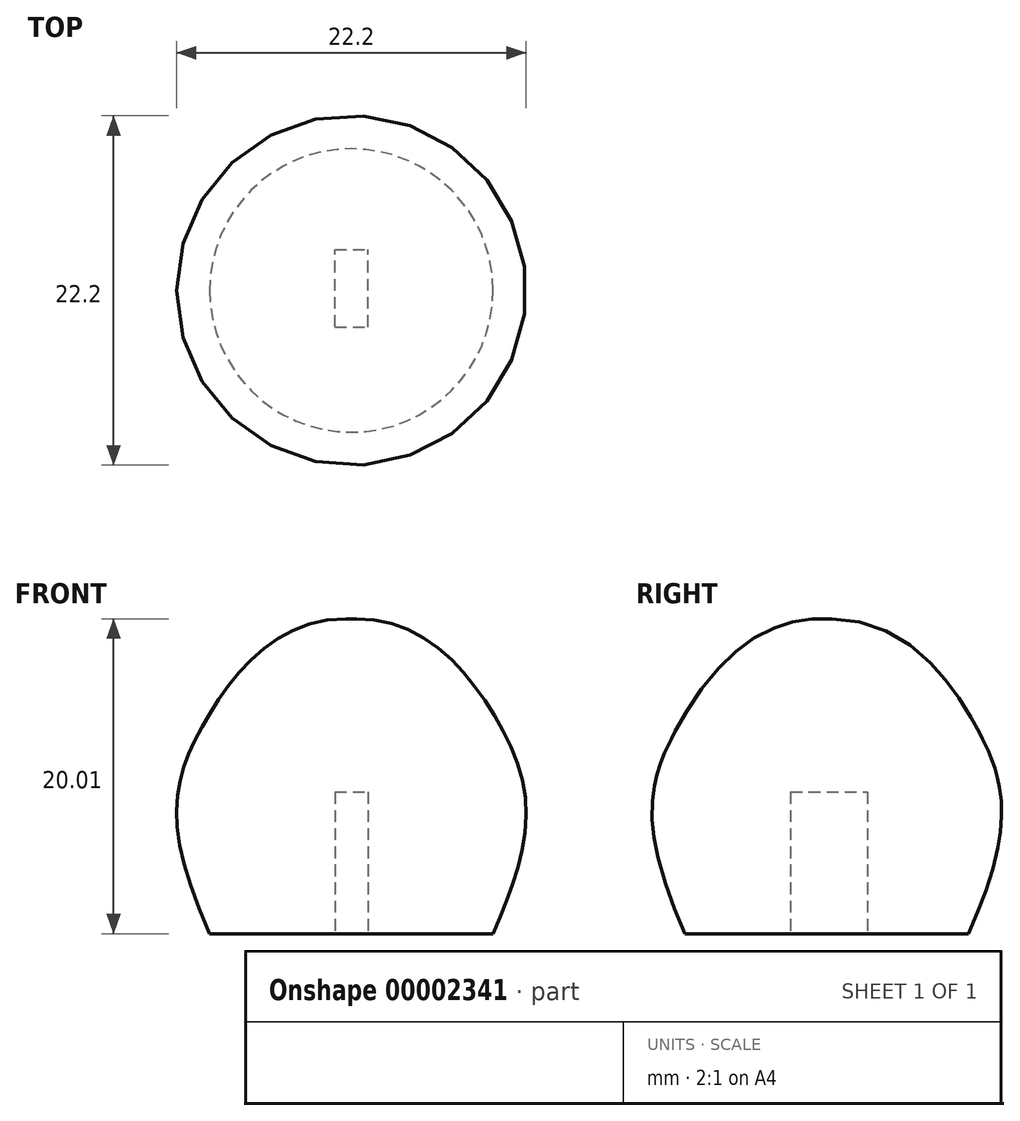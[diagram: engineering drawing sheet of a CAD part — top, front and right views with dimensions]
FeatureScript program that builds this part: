
annotation { "Feature Type Name" : "Feature", "Feature Type Description" : "" }
export const myFeature = defineFeature(function(context is Context, id is Id, definition is map)
    precondition{}
    {
        {
            var Q0;
            Q0=qCreatedBy(makeId("Front.planeOp"),FACE);
            var sketch = newSketch(context, id + "F0", { "sketchPlane" : qUnion([Q0])});
            skFitSpline(sketch, "E0", {"points": [v(-9, 0) * mm, v(-9.53, 13.06) * mm, v(0, 20) * mm], "startDerivative": vector(-17.7, 39.61) * mm, "endDerivative": vector(29.7, -1.1) * mm});
            skLineSegment(sketch, "E1", {"start": v(0, 20) * mm, "end": v(0, 0) * mm});
            skLineSegment(sketch, "E2", {"start": v(0, 0) * mm, "end": v(-9, 0) * mm});
            skSolve(sketch);
        }
        {
            var Q0;
            Q0 = qSketchRegion(id + "F0", true);
            var Q1;
            Q1=sQuery(id+"F0.wireOp",EDGE,"E1");
            revolve(context, id + "F1", {"entities" : qUnion([Q0]), "axis" : qUnion([Q1]), "revolveType" : RevolveType.FULL});
        }
        {
            var Q0;
            Q0=makeQuery(id+"F1.opRevolve","SWEPT_FACE",FACE,{"disambiguationData":[OSD([sQuery(id+"F0.wireOp",EDGE,"E2")])]});
            var sketch = newSketch(context, id + "F2", { "sketchPlane" : qUnion([Q0])});
            skLineSegment(sketch, "E3.bottom", {"start": v(-1.05, 2.3) * mm, "end": v(1.05, 2.3) * mm});
            skLineSegment(sketch, "E3.top", {"start": v(-1.05, -2.6) * mm, "end": v(1.05, -2.6) * mm});
            skLineSegment(sketch, "E3.left", {"start": v(-1.05, 2.3) * mm, "end": v(-1.05, -2.6) * mm});
            skLineSegment(sketch, "E3.right", {"start": v(1.05, 2.3) * mm, "end": v(1.05, -2.6) * mm});
            skSolve(sketch);
        }
        {
            var Q0;
            Q0 = qSketchRegion(id + "F2", true);
            extrude(context, id + "F3", {"entities" : qUnion([Q0]), "operationType" : NewBodyOperationType.REMOVE, "oppositeDirection" : true, "depth" : 9 * mm});
        }
    });
